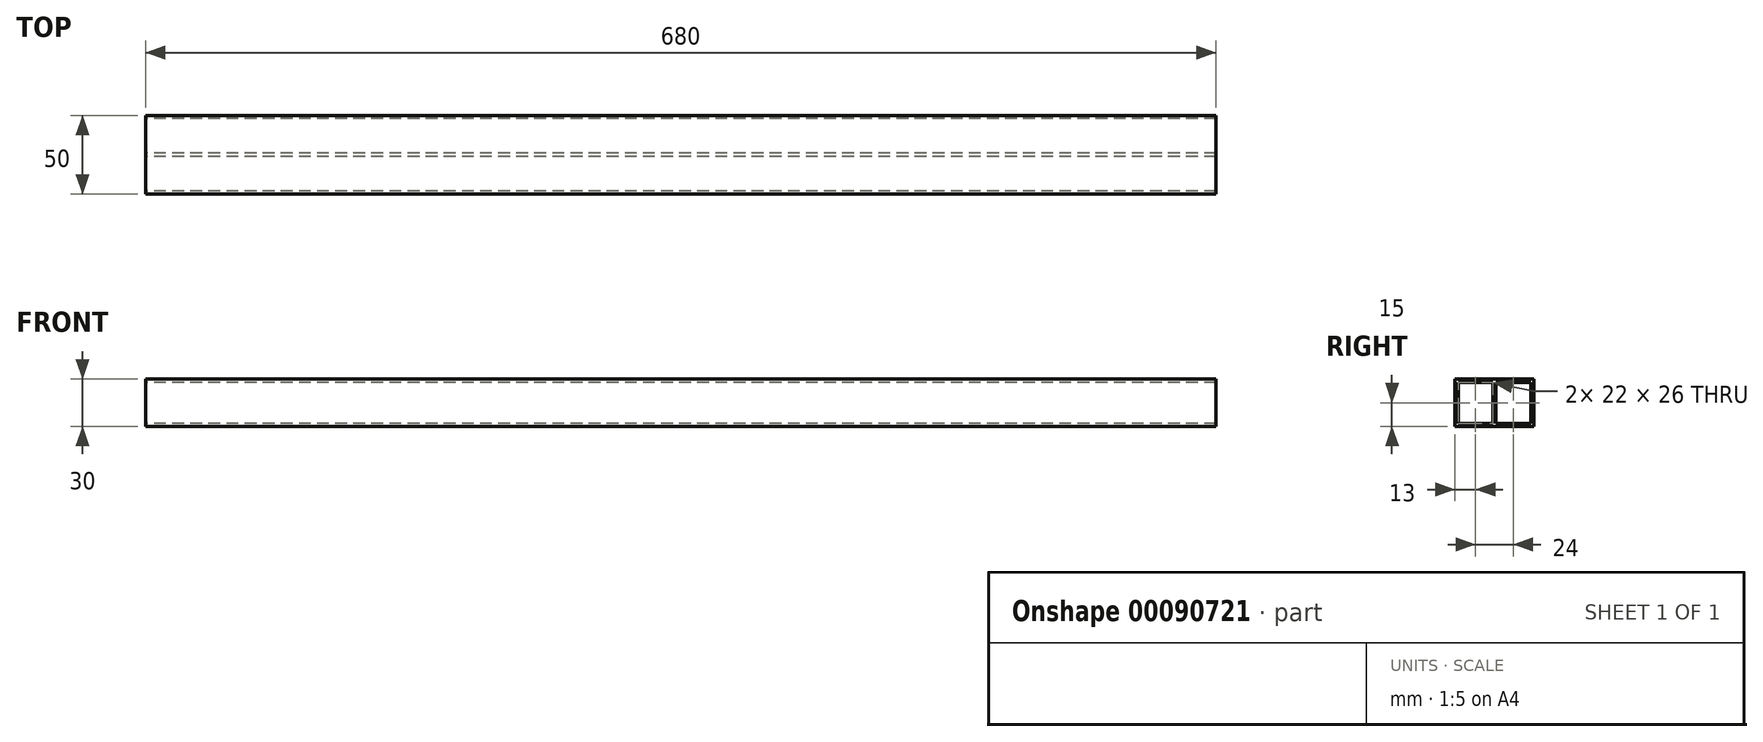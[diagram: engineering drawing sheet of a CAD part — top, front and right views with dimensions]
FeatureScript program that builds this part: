
annotation { "Feature Type Name" : "Feature", "Feature Type Description" : "" }
export const myFeature = defineFeature(function(context is Context, id is Id, definition is map)
    precondition{}
    {
        {
            var Q0;
            Q0=qCreatedBy(makeId("Right.planeOp"),FACE);
            var sketch = newSketch(context, id + "F0", { "sketchPlane" : qUnion([Q0])});
            skLineSegment(sketch, "E0", {"start": v(-25, 15) * mm, "end": v(25, 15) * mm});
            skLineSegment(sketch, "E1", {"start": v(-25, 15) * mm, "end": v(-25, -15) * mm});
            skLineSegment(sketch, "E2", {"start": v(-25, -15) * mm, "end": v(25, -15) * mm});
            skLineSegment(sketch, "E3", {"start": v(25, -15) * mm, "end": v(25, 15) * mm});
            skLineSegment(sketch, "E4", {"start": v(0, 15) * mm, "end": v(0, -15) * mm, "construction": true});
            skLineSegment(sketch, "E5.bottom", {"start": v(-23, 13) * mm, "end": v(-1, 13) * mm});
            skLineSegment(sketch, "E5.top", {"start": v(-23, -13) * mm, "end": v(-1, -13) * mm});
            skLineSegment(sketch, "E5.left", {"start": v(-23, 13) * mm, "end": v(-23, -13) * mm});
            skLineSegment(sketch, "E5.right", {"start": v(-1, 13) * mm, "end": v(-1, -13) * mm});
            skLineSegment(sketch, "E6.MirrorCS", {"start": v(23, -13) * mm, "end": v(1, -13) * mm});
            skLineSegment(sketch, "E7.MirrorCS", {"start": v(23, 13) * mm, "end": v(23, -13) * mm});
            skLineSegment(sketch, "E8.MirrorCS", {"start": v(23, 13) * mm, "end": v(1, 13) * mm});
            skLineSegment(sketch, "E9.MirrorCS", {"start": v(1, 13) * mm, "end": v(1, -13) * mm});
            skLineSegment(sketch, "E10", {"start": v(-25, 0) * mm, "end": v(25, 0) * mm, "construction": true});
            skSolve(sketch);
        }
        {
            var Q0;
            Q0 = qSketchRegion(id + "F0", true);
            extrude(context, id + "F1", {"entities" : qUnion([Q0]), "depth" : 680 * mm});
        }
    });
